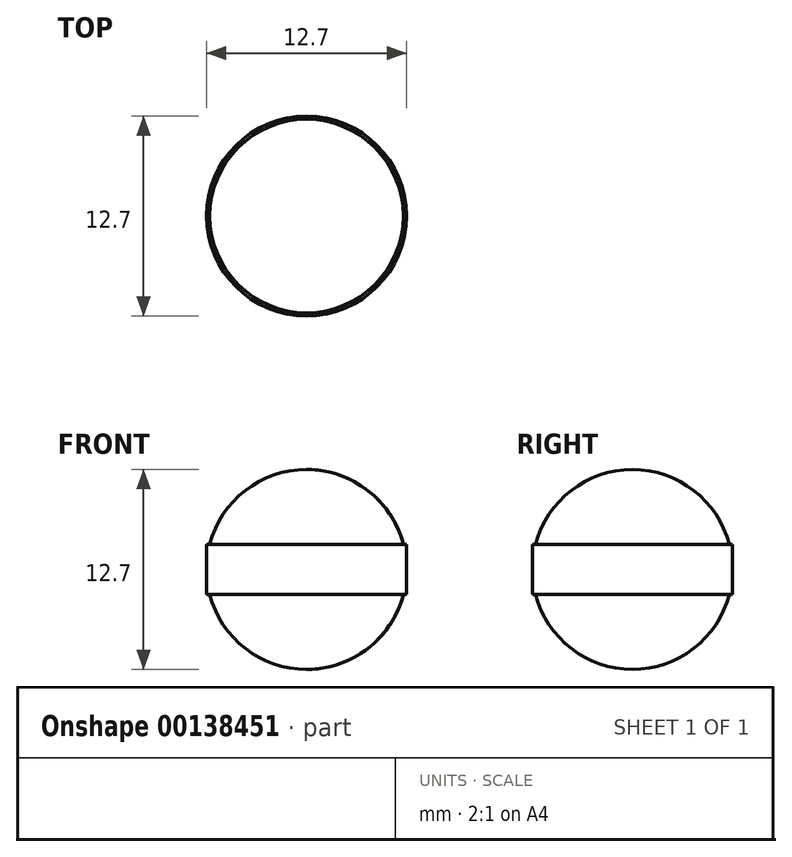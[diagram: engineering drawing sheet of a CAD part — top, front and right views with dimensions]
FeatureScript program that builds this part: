
annotation { "Feature Type Name" : "Feature", "Feature Type Description" : "" }
export const myFeature = defineFeature(function(context is Context, id is Id, definition is map)
    precondition{}
    {
        {
            var Q0;
            Q0=qCreatedBy(makeId("Top.planeOp"),FACE);
            var sketch = newSketch(context, id + "F0", { "sketchPlane" : qUnion([Q0])});
            skCircle(sketch, "E0", {"center": v(0, 0) * mm, "radius": 6.35 * mm});
            skSolve(sketch);
        }
        {
            var Q0;
            Q0 = qSketchRegion(id + "F0", true);
            extrude(context, id + "F1", {"entities" : qUnion([Q0]), "endBound" : BoundingType.SYMMETRIC, "depth" : 12.7 * mm});
        }
        {
            var Q0;
            Q0=makeQuery(id+"F1.opExtrude","CAP_EDGE",EDGE,{"disambiguationData":[OSD([sQuery(id+"F0.wireOp",EDGE,"E0")])],"isStart":false});
            var Q1;
            Q1=makeQuery(id+"F1.opExtrude","CAP_EDGE",EDGE,{"disambiguationData":[OSD([sQuery(id+"F0.wireOp",EDGE,"E0")])],"isStart":true});
            fillet(context, id + "F2", {"entities" : qUnion([Q0, Q1]), "radius" : 6.35 * mm, "tangentPropagation" : true, "allowEdgeOverflow" : false});
        }
        {
            var Q0;
            Q0=qCreatedBy(makeId("Top.planeOp"),FACE);
            var sketch = newSketch(context, id + "F3", { "sketchPlane" : qUnion([Q0])});
            skCircle(sketch, "E1", {"center": v(0, 0) * mm, "radius": 6.35 * mm});
            skSolve(sketch);
        }
        {
            var Q0;
            Q0 = qSketchRegion(id + "F3", true);
            extrude(context, id + "F4", {"entities" : qUnion([Q0]), "operationType" : NewBodyOperationType.ADD, "endBound" : BoundingType.SYMMETRIC, "depth" : 3.17 * mm});
        }
    });
